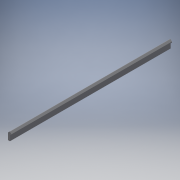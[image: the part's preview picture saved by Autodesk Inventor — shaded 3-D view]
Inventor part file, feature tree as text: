
AUTODESK INVENTOR PART (.ipt)
format: ipt  version: 2017.1 (Build 211199000, 199)  size: 118,272 bytes
history: native  units: in
note: dims shown in document units (in); Inventor stores cm internally (conversion verified against a paired STEP export)
features: fillet x1, other x1, imported_body x1
ambient origin geometry x8: Origin, YZ Plane, XZ Plane, XY Plane, X Axis, Y Axis, Z Axis, Center Point
bodies: Body1 (feature_tree)
feature tree (3):
  fillet  "Fillet1"  [1 undecoded]
  other  "BWC-T2-11"
  imported_body  "Base1"
note: 1 required parameter value undecoded (feature->parameter linkage not recoverable at this tier; creation-order binding heuristic only, values carry confidence <= 0.55)
